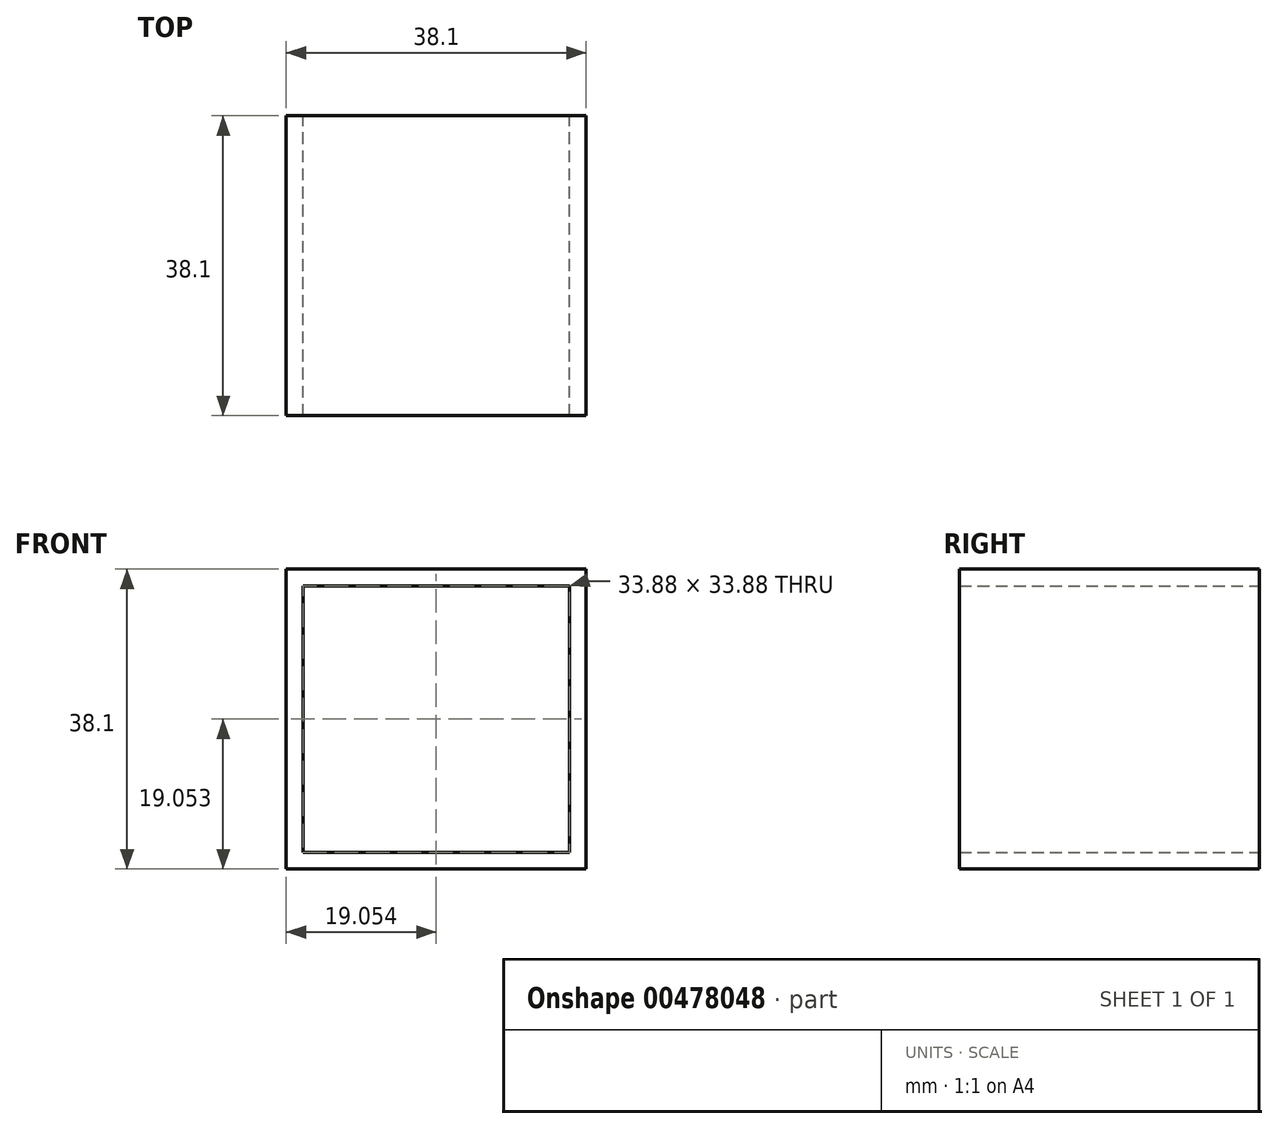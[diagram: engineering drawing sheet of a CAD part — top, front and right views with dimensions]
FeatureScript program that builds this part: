
annotation { "Feature Type Name" : "Feature", "Feature Type Description" : "" }
export const myFeature = defineFeature(function(context is Context, id is Id, definition is map)
    precondition{}
    {
        {
            var Q0;
            Q0=qCreatedBy(makeId("Front.planeOp"),FACE);
            var sketch = newSketch(context, id + "F0", { "sketchPlane" : qUnion([Q0])});
            skLineSegment(sketch, "E0.bottom", {"start": v(-32.36, 47.21) * mm, "end": v(5.74, 47.21) * mm});
            skLineSegment(sketch, "E0.top", {"start": v(-32.36, 9.11) * mm, "end": v(5.74, 9.11) * mm});
            skLineSegment(sketch, "E0.left", {"start": v(-32.36, 47.21) * mm, "end": v(-32.36, 9.11) * mm});
            skLineSegment(sketch, "E0.right", {"start": v(5.74, 47.21) * mm, "end": v(5.74, 9.11) * mm});
            skLineSegment(sketch, "E1.0", {"start": v(-30.25, 11.22) * mm, "end": v(3.64, 11.22) * mm});
            skLineSegment(sketch, "E1.1", {"start": v(-30.25, 45.1) * mm, "end": v(-30.25, 11.22) * mm});
            skLineSegment(sketch, "E1.2", {"start": v(-30.25, 45.1) * mm, "end": v(3.64, 45.1) * mm});
            skLineSegment(sketch, "E1.3", {"start": v(3.64, 45.1) * mm, "end": v(3.64, 11.22) * mm});
            skSolve(sketch);
        }
        {
            var Q0;
            Q0=qSketchRegion(id+"F0",true);
            extrude(context, id + "F1", {"entities" : qUnion([Q0]), "depth" : 38.1 * mm});
        }
    });
